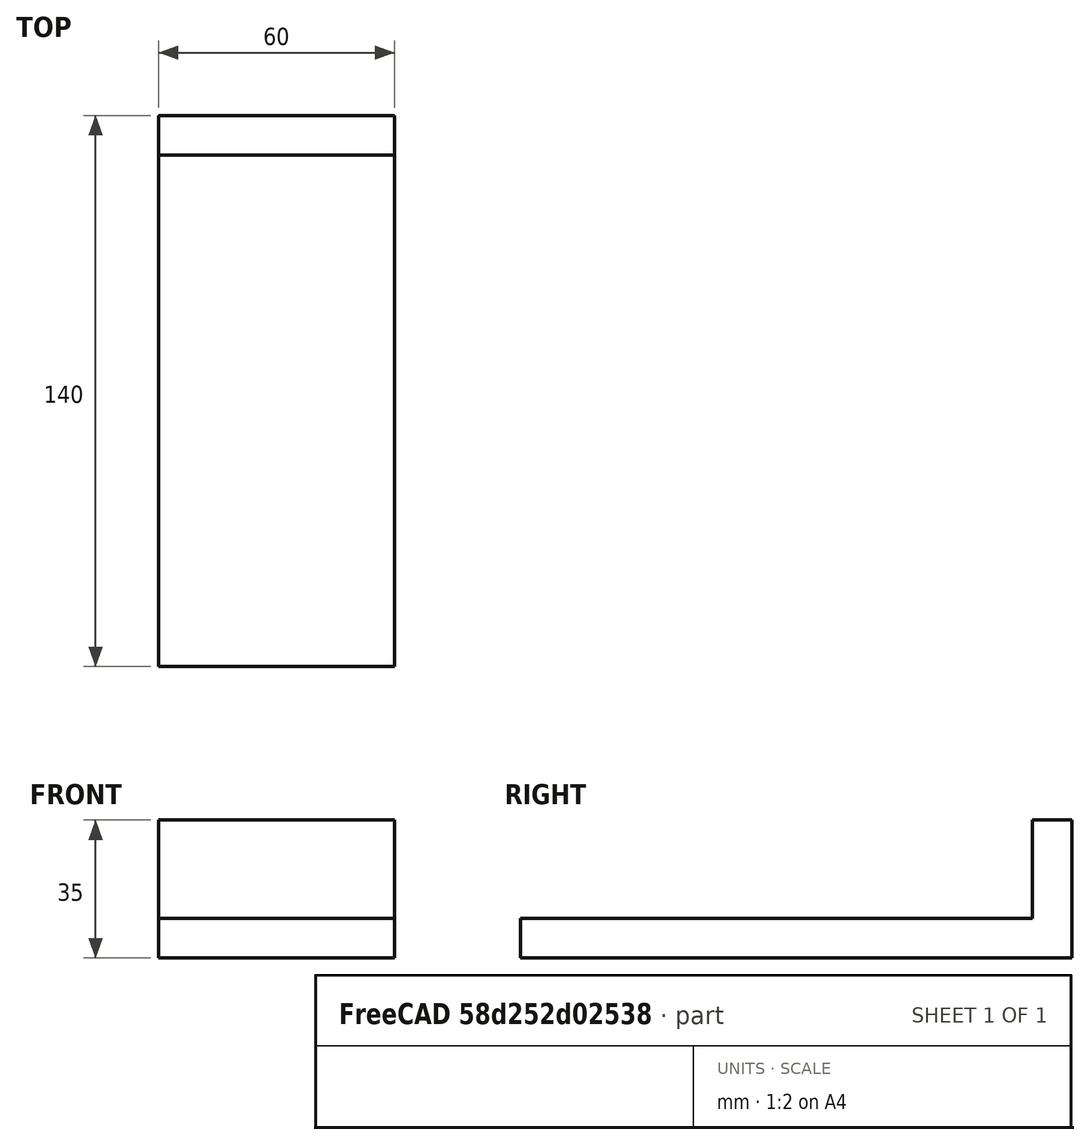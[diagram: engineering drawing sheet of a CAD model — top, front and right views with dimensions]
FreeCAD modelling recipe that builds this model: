
FCSTD DOCUMENT  (FreeCAD 0.20R29410 (Git))
Label: base_bateria
License: All rights reserved
LicenseURL: http://en.wikipedia.org/wiki/All_rights_reserved
objects: Part::Box×3, Part::MultiFuse×2
note: 5 computed .brp shape members not serialized (recipe doc carries the construction recipe); baked Part::Feature solids carry a one-line shape summary decoded from their .brp

FEATURE [Part::Box] Box  label="Cubo"
  AttacherType = Attacher::AttachEngine3D
  Height = 10
  Length = 60
  Placement = pos=(0,-90,0) rot=(0,0,1;0rad)
  Width = 100
FEATURE [Part::Box] Box001  label="Cubo001"
  AttacherType = Attacher::AttachEngine3D
  Height = 25
  Length = 60
  Placement = pos=(0,0,10) rot=(0,0,1;0rad)
  Width = 10
FEATURE [Part::MultiFuse] Fusion
  Shapes = -> [Box,Box001]
FEATURE [Part::Box] Box002  label="Cubo002"
  AttacherType = Attacher::AttachEngine3D
  Height = 10
  Length = 60
  Placement = pos=(0,-130,0) rot=(0,0,1;0rad)
  Width = 40
FEATURE [Part::MultiFuse] Fusion001
  Shapes = -> [Fusion,Box002]
